# Revit family: LAMP_OCULT DOWNLIGHT TRIMLESS WIDE FLOOD (DALI)
name_source: partatom
category: Modelos genéricos
revit_build: Autodesk Revit 2015 (Build: 20140606_1530(x64)
units: mm (PartAtom-declared; Revit-internal decimal feet)

## types (10) — shared parameters
CRI = 80
Elevación por defecto = 1219 mm
Fabricante = LAMP
Finish = Texturised black
Gear = Adjustable DALI
IEE = A+
Installation instructions = https://www.lamp.es
Insulation class = II
LED Lifetime = 50.000 L90 B10
Lamp = HIGH POWER LED
Last update = 12/02/2019
Luminaire type = Indoor - Downlight
MacAdam = 3
Manufacturer URL = http://www.lamp.es
Manufacturer country = Spain
Manufacturer name = LAMP
Model explanation = Availability of change reflector color when placed in a project.
Photometric web file = Perfil luminico TRIM WF : 2 MOD 366LM 3000 WIDE FLOOD BLACK
Product URL = https://www.lamp.es
Product datasheet = http://www.lamp.es
Protection rating = IP20
Type = HI POWER NICHIA
UGR = 16

## per-type parameters (varying)
| type | Descripción | Dimensions | Efficacy | Initial color | Initial intensity | Modelo | Number of reflectors | Plum | Power | Power Supply | Product code | Recessed dimensions | Weight |
| 2 MOD 366LM 3000 WIDE FLOOD BLACK | OCULT TRIM 2 400 WW WFL BK. | 66 x 34 x73 | 73 lm/W | 3000 K | 366 lm | OD1TR204WF830NB | 2 | 5 W | 4 W | 100-240V 50/60Hz | OD1TR204WF830NB | 74 x 55 | 0.36 kg |
| 2 MOD 366LM 4000 WIDE FLOOD BLACK | OCULT TRIM 2 400 NW WFL BK. | 66 x 34 x73 | 73 lm/W | 4000 K | 366 lm | OD1TR204WF840NB | 2 | 5 W | 4 W | 100-240V 50/60Hz | OD1TR204WF840NB | 74 x 55 | 0.36 kg |
| 3 MOD 549LM 3000 WIDE FLOOD BLACK | OCULT TRIM 3 600 WW WFL BK. | 99 x 34 x73 | 69 lm/W | 3000 K | 549 lm | OD1TR306WF830NB | 2 | 8 W | 6 W | 100-240V 50/60Hz | OD1TR306WF830NB | 107 x 55 | 0.46 kg |
| 3 MOD 549LM 4000 WIDE FLOOD BLACK | OCULT TRIM 3 600 NW WFL BK. | 99 x 34 x73 | 69 lm/W | 4000 K | 549 lm | OD1TR306WF840NB | 2 | 8 W | 6 W | 100-240V 50/60Hz | OD1TR306WF840NB | 107 x 55 | 0.46 kg |
| 6 MOD 1098LM 3000 WIDE FLOOD BLACK | OCULT TRIM 6 1200 WW WFL BK. | 198 x 34 x73 | 78 lm/W | 3000 K | 1098 lm | OD1TR612WF830NB | 3 | 14 W | 12 W | 220-240V 50/60Hz | OD1TR612WF830NB | 207 x 55 | 0.84 kg |
| 6 MOD 1098LM 4000 WIDE FLOOD BLACK | OCULT TRIM 6 1200 NW WFL BK. | 198 x 34 x73 | 78 lm/W | 4000 K | 1098 lm | OD1TR612WF840NB | 3 | 14 W | 12 W | 220-240V 50/60Hz | OD1TR612WF840NB | 207 x 55 | 0.84 kg |
| 9 MOD 1647LM 3000 WIDE FLOOD BLACK | OCULT TRIM 9 1800 WW WFL BK. | 297 x 34 x73 | 82 lm/W | 3000 K | 1647 lm | OD1TR918WF830NB | 3 | 20 W | 18 W | 120-277V 50/60Hz | OD1TR918WF830NB | 307 x 55 | 1.13 kg |
| 9 MOD 1647LM 4000 WIDE FLOOD BLACK | OCULT TRIM 9 1800 NW WFL BK. | 297 x 34 x73 | 82 lm/W | 4000 K | 1647 lm | OD1TR918WF840NB | 3 | 20 W | 18 W | 120-277V 50/60Hz | OD1TR918WF840NB | 307 x 55 | 1.13 kg |
| 12 MOD 2196LM 3000 WIDE FLOOD BLACK | OCULT TRIM 12 2400 WW WFL BK. | 396 x 34 x73 | 81 lm/W | 3000 K | 2196 lm | OD1TR1222WF830NB | 6 | 27 W | 24 W | 120-240V 50/60Hz | OD1TR1222WF830NB | 407 x 55 | 1.50 kg |
| 12 MOD 2196LM 4000 WIDE FLOOD BLACK | OCULT TRIM 12 2400 NW WFL BK. | 396 x 34 x73 | 82 lm/W | 4000 K | 2196 lm | OD1TR1222WF840NB | 6 | 27 W | 24 W | 120-240V 50/60Hz | OD1TR1222WF840NB | 407 x 55 | 1.50 kg |

## geometry (parser evidence)
native form markers: Blend x2
no freeform markers — native parametric forms only
